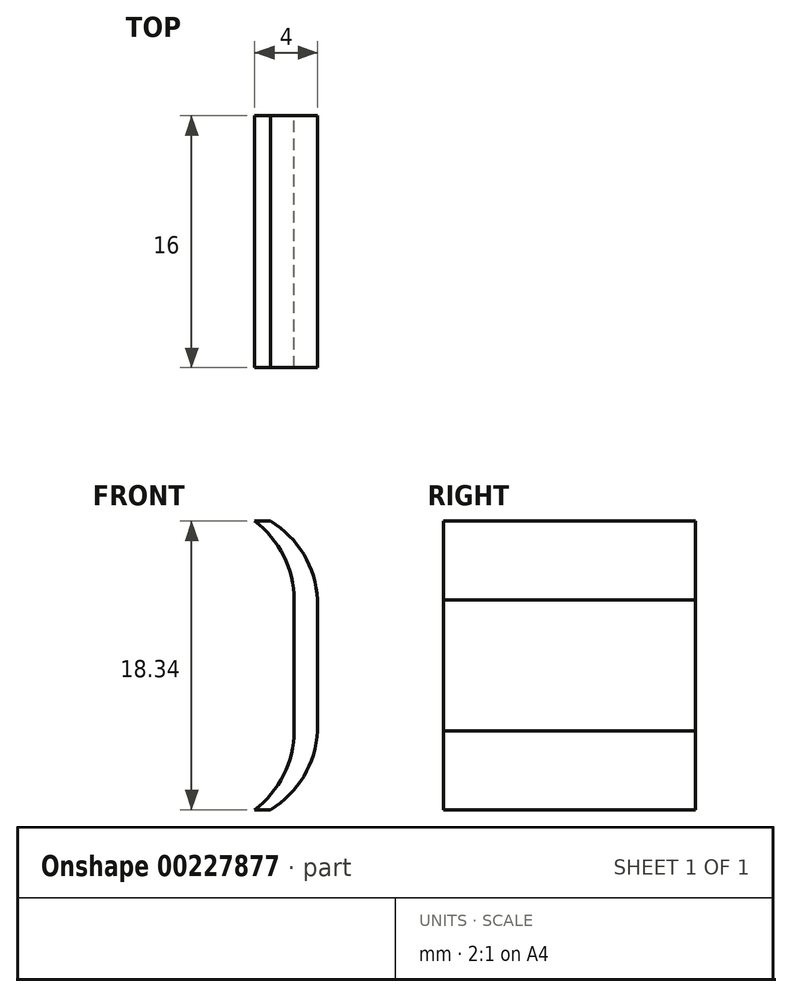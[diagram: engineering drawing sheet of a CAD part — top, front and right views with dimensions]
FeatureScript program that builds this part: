
annotation { "Feature Type Name" : "Feature", "Feature Type Description" : "" }
export const myFeature = defineFeature(function(context is Context, id is Id, definition is map)
    precondition{}
    {
        {
            var Q0;
            Q0=qCreatedBy(makeId("Front.planeOp"),FACE);
            var sketch = newSketch(context, id + "F0", { "sketchPlane" : qUnion([Q0])});
            skLineSegment(sketch, "E0", {"start": v(0, 0) * mm, "end": v(0, 55) * mm});
            skLineSegment(sketch, "E1", {"start": v(0, 55) * mm, "end": v(0, 44) * mm});
            skLineSegment(sketch, "E2", {"start": v(0, 44) * mm, "end": v(-15.4, 44) * mm});
            skLineSegment(sketch, "E3", {"start": v(-15.4, 44) * mm, "end": v(-16.9, 44) * mm});
            skLineSegment(sketch, "E4.top", {"start": v(-15.4, 52.34) * mm, "end": v(-16.9, 52.34) * mm});
            skLineSegment(sketch, "E4.left", {"start": v(-15.4, 44) * mm, "end": v(-15.4, 52.34) * mm});
            skLineSegment(sketch, "E4.right", {"start": v(-16.9, 44) * mm, "end": v(-16.9, 52.34) * mm});
            skArc(sketch, "E5", {"start": v(-18.4, 39) * mm, "mid": v(-16.28, 41.13) * mm, "end": v(-15.4, 44) * mm});
            skArc(sketch, "E6", {"start": v(-19.4, 39) * mm, "mid": v(-17.56, 41.2) * mm, "end": v(-16.9, 44) * mm});
            skLineSegment(sketch, "E7", {"start": v(-19.4, 39) * mm, "end": v(-18.4, 39) * mm});
            skLineSegment(sketch, "E8", {"start": v(-16.9, 48.17) * mm, "end": v(-15.4, 48.17) * mm});
            skArc(sketch, "E9.MirrorCS", {"start": v(-19.4, 57.34) * mm, "mid": v(-17.56, 55.14) * mm, "end": v(-16.9, 52.34) * mm});
            skArc(sketch, "E10.MirrorCS", {"start": v(-18.4, 57.34) * mm, "mid": v(-16.28, 55.22) * mm, "end": v(-15.4, 52.34) * mm});
            skLineSegment(sketch, "E11.MirrorCS", {"start": v(-19.4, 57.34) * mm, "end": v(-18.4, 57.34) * mm});
            skSolve(sketch);
        }
        {
            var Q0;
            Q0=qSketchRegion(id+"F0",true);
            extrude(context, id + "F1", {"entities" : qUnion([Q0]), "depth" : 8 * mm, "hasSecondDirection" : true, "secondDirectionOppositeDirection" : true, "secondDirectionDepth" : 8 * mm});
        }
    });
